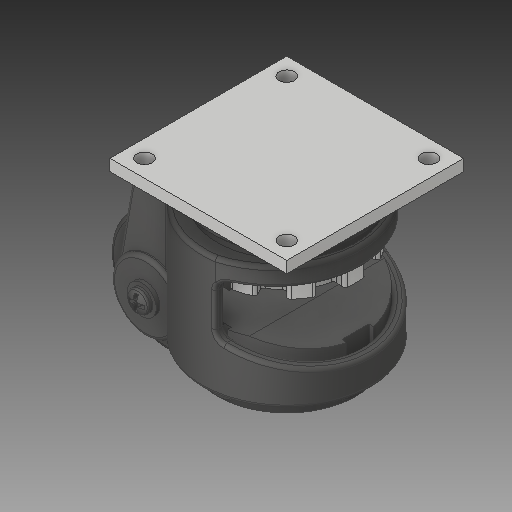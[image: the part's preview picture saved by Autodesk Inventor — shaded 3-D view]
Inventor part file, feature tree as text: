
AUTODESK INVENTOR PART (.ipt)
format: ipt  version: 2019 (Build 230136000, 136)  size: 1,201,152 bytes
history: mixed  units: in
note: dims shown in document units (in); Inventor stores cm internally (conversion verified against a paired STEP export)
features: other x3, extrude x2, fillet x1, pattern_circular x1, imported_body x1
ambient origin geometry x8: Origin, YZ Plane, XZ Plane, XY Plane, X Axis, Y Axis, Z Axis, Center Point
bodies: Solid1 (imported_parasolid), Solid2 (imported_parasolid), Solid3 (imported_parasolid), Solid4 (imported_parasolid), Solid5 (imported_parasolid), Solid6 (imported_parasolid), Solid7 (imported_parasolid)
feature tree (8):
  fillet  "Fillet2"  [1 undecoded]
  extrude  "Extrude3"  [1 undecoded]
  extrude  "Extrude28"  [1 undecoded]
  other  "Cut-Sweep1"
  pattern_circular  "CirPattern2"
  other  "Cut-Extrude1"
  other  "Boss-Extrude1"
  imported_body  NMx_Import_Brep_tag  [imported B-rep: ~34 faces, bbox_mm=None]
note: 3 required parameter values undecoded (feature->parameter linkage not recoverable at this tier; creation-order binding heuristic only, values carry confidence <= 0.55)
